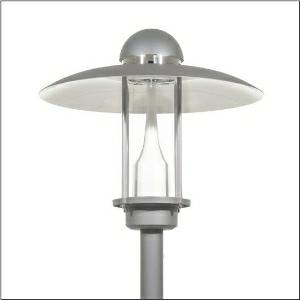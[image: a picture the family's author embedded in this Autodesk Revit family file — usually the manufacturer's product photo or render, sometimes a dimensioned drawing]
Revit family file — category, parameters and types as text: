
# Revit family: city-light_elegance_iq___st1_2a_5xa5265mf14h_1b27
name_source: partatom
category: Lighting Fixtures
units: mm (PartAtom-declared; Revit-internal decimal feet)

## family parameters
Cut with Voids When Loaded = No
Host = Face
Light Source = No
Part Type = Normal
Room Calculation Point = No
Round Connector Dimension = Use Diameter
Shared = No

## types (1)
- --- (1 x LED, 1470 lm, 11.8 W, 2700K)
    Apparent Load = 12 VA
    CIE Flux Codes = 22 62 94 98 100
    Color Rendering = 70
    Color Temperature = 2700K
    Default Elevation = 1800 mm
    Description = City-Light Elegance iQ, mast luminaire, Module 540 iQ-SR, primary light control with 3 zone facetted reflector, of plastic, silver coated, highly specular, structured, primary optical cover: cover, of PMMA, transparent, light distribution: ST1.2a, light emission: direct distribution, primary light characteristic: asymmetric, installation type: post-top, LED, High Power LED, rated luminous flux: 1.470lm, luminous efficacy: 124lm/W, light colour: 727, colour temperature: 2700K, control gear: ECG iQ, control: presetting dimming logarithmic, Street-Remote, Auto-Match, Temp-Guard, Lumen-Switch, Night-Set, Smart-Wire, Light-Fading, Desk-Remote (wireless, voltage-free reading and setting of iQ features in the workshop via application-optimized NFC function/RFID function), optimised constant luminous flux control (CLO 2.0), with terminal, 6-pole, max. 2.5mm², mains connection: 220..240V, AC, 50/60Hz, start of lifetime: 12W, end of lifetime: 12W, reduction: 6W, luminaire housing, upper part, of aluminium, coated, Siteco® metallic grey (DB 702S), diameter: 750mm, height: 675mm, spigot size: d x l = 76 x 70mm (post-top) | with reducer (optional accessory) 60 x 70mm, post-top mast mounting element, of diecast aluminium, coated, Siteco® metallic grey (DB 702S), Module 540 iQ-SR, traffic white (RAL 9016), equipment: standard, protection rating (complete): IP65, insulation class (complete): insulation class II (safety insulation), certification: CE, ENEC, VDE, packaging unit: 1 piece

Light Distribution: ST1.2a
    Height = 675 mm
    Lamp = 1 x LED
    Lamp Light Flux = 1470 lm
    Lamp Power = 11.8 W
    Lamp count = 1
    Length = 750 mm
    Luminous efficacy = 125 lm/W
    Manufacturer = Siteco
    ModVariant = No
    Model = 5XA5265MF14H
    Number of Poles = 1
    OnlyDefault = Yes
    Power Factor = 1
    Product Name = City-Light Elegance iQ | ST1.2a
    Product group = mast luminaire | pylon top
    ProductGroupID = 6100
    Protection Class = Protection class II
    Protection Degree = IP 65
    RLX_Detail_Level = 1
    RlxData = <blob elided: 99861 chars, md5=90091dec>
    Socket = socket
    Standby Power = 0 W
    System Light Flux = 1470 lm
    System Power = 12 W
    Type Comments = factory setting: luminous flux: 100 % | dim-lin: 254 | 472 mA
    Type Image = l_1006912.jpg
    URL = http://relux.com
    VarID = @adj_063089
    Voltage = 0 V
    Weight = 0.00 kg
    Width = 0 mm  [stored 0 ft]

note: [stored X ft] marks values corroborated as IEEE doubles in the binary element streams (Revit-internal decimal feet)

## geometry (parser evidence)
native form markers: Blend x4, Sweep x10
no freeform markers — native parametric forms only
